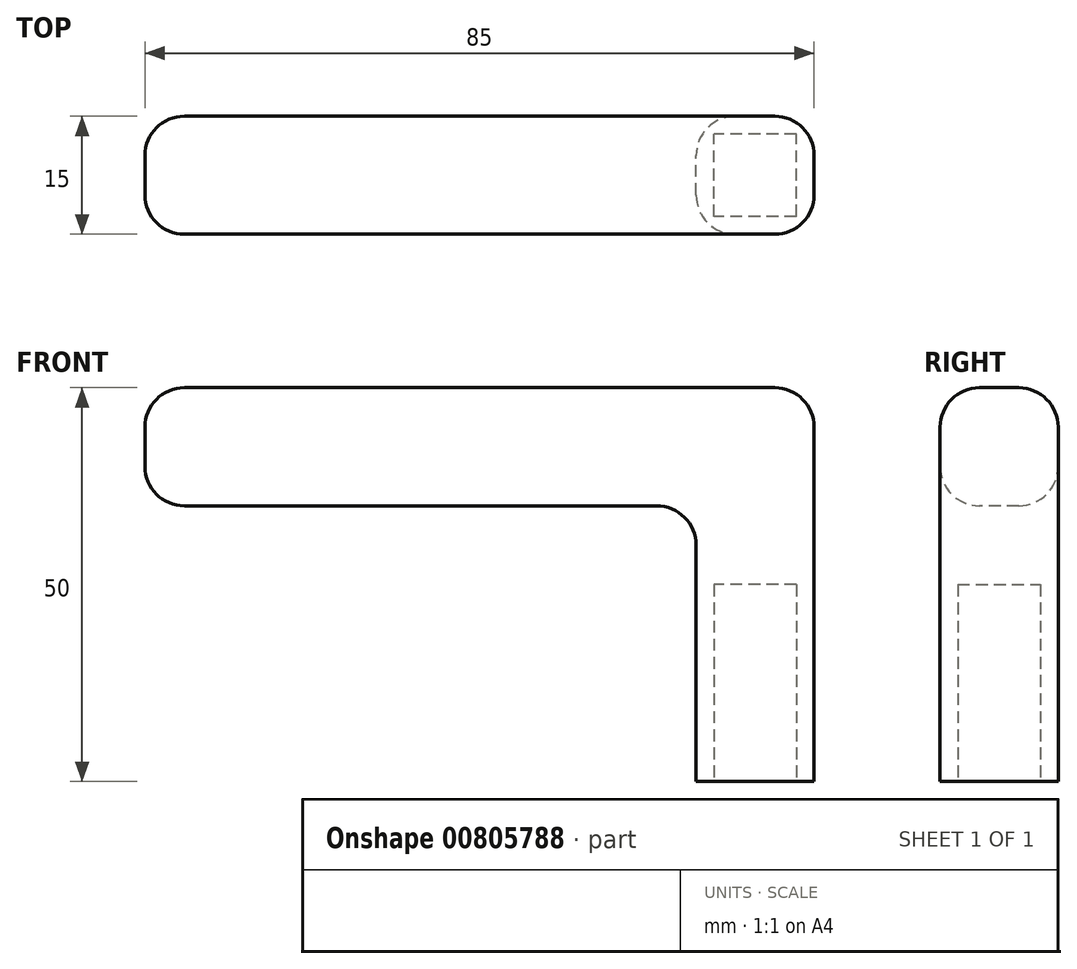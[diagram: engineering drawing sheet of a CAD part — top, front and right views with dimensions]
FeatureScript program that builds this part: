
annotation { "Feature Type Name" : "Feature", "Feature Type Description" : "" }
export const myFeature = defineFeature(function(context is Context, id is Id, definition is map)
    precondition{}
    {
        {
            var Q0;
            Q0=qCreatedBy(makeId("Top.planeOp"),FACE);
            var sketch = newSketch(context, id + "F0", { "sketchPlane" : qUnion([Q0])});
            skLineSegment(sketch, "E0.bottom", {"start": v(5.25, -5.25) * mm, "end": v(-5.26, -5.25) * mm});
            skLineSegment(sketch, "E0.top", {"start": v(5.25, 5.26) * mm, "end": v(-5.25, 5.26) * mm});
            skLineSegment(sketch, "E0.left", {"start": v(5.25, -5.25) * mm, "end": v(5.25, 5.25) * mm});
            skLineSegment(sketch, "E0.right", {"start": v(-5.25, -5.25) * mm, "end": v(-5.25, 5.25) * mm});
            skPoint(sketch, "E0.middle", {"position": v(0, 0) * mm});
            skLineSegment(sketch, "E1.bottom", {"start": v(7.5, -7.5) * mm, "end": v(-7.5, -7.5) * mm});
            skLineSegment(sketch, "E1.top", {"start": v(7.5, 7.5) * mm, "end": v(-7.5, 7.5) * mm});
            skLineSegment(sketch, "E1.left", {"start": v(7.5, -7.5) * mm, "end": v(7.5, 7.5) * mm});
            skLineSegment(sketch, "E1.right", {"start": v(-7.5, -7.5) * mm, "end": v(-7.5, 7.5) * mm});
            skSolve(sketch);
        }
        {
            var Q0;
            Q0 = qSketchRegion(id + "F0", true);
            extrude(context, id + "F1", {"entities" : qUnion([Q0]), "depth" : 25 * mm, "offsetDistance" : 25 * mm});
        }
        {
            var Q0;
            Q0=makeQuery(id+"F1.opExtrude","CAP_FACE",FACE,{"disambiguationData":[OSD([sQuery(id+"F0.wireOp",EDGE,"E0.bottom"),sQuery(id+"F0.wireOp",EDGE,"E0.top"),sQuery(id+"F0.wireOp",EDGE,"E0.left"),sQuery(id+"F0.wireOp",EDGE,"E0.right"),sQuery(id+"F0.wireOp",EDGE,"E1.bottom"),sQuery(id+"F0.wireOp",EDGE,"E1.top"),sQuery(id+"F0.wireOp",EDGE,"E1.left"),sQuery(id+"F0.wireOp",EDGE,"E1.right")])],"isStart":false});
            var sketch = newSketch(context, id + "F2", { "sketchPlane" : qUnion([Q0])});
            skLineSegment(sketch, "E2.bottom", {"start": v(7.5, -7.5) * mm, "end": v(-7.5, -7.5) * mm});
            skLineSegment(sketch, "E2.top", {"start": v(7.5, 7.5) * mm, "end": v(-7.5, 7.5) * mm});
            skLineSegment(sketch, "E2.left", {"start": v(7.5, -7.5) * mm, "end": v(7.5, 7.5) * mm});
            skLineSegment(sketch, "E2.right", {"start": v(-7.5, -7.5) * mm, "end": v(-7.5, 7.5) * mm});
            skPoint(sketch, "E2.middle", {"position": v(0, 0) * mm});
            skSolve(sketch);
        }
        {
            var Q0;
            Q0 = qSketchRegion(id + "F2", true);
            extrude(context, id + "F3", {"entities" : qUnion([Q0]), "operationType" : NewBodyOperationType.ADD, "depth" : 25 * mm, "offsetDistance" : 25 * mm});
        }
        {
            var Q0;
            Q0=makeQuery(id+"F3.boolean.opBoolean","MERGE",FACE,{"derivedFrom":[makeQuery(id+"F1.opExtrude","SWEPT_FACE",FACE,{"disambiguationData":[OSD([sQuery(id+"F0.wireOp",EDGE,"E1.right")])]}),makeQuery(id+"F3.opExtrude","SWEPT_FACE",FACE,{"disambiguationData":[OSD([sQuery(id+"F2.wireOp",EDGE,"E2.right")])]})]});
            var sketch = newSketch(context, id + "F4", { "sketchPlane" : qUnion([Q0])});
            skLineSegment(sketch, "E3.bottom", {"start": v(-7.5, 50) * mm, "end": v(7.5, 50) * mm});
            skLineSegment(sketch, "E3.top", {"start": v(-7.5, 35) * mm, "end": v(7.5, 35) * mm});
            skLineSegment(sketch, "E3.left", {"start": v(-7.5, 50) * mm, "end": v(-7.5, 35) * mm});
            skLineSegment(sketch, "E3.right", {"start": v(7.5, 50) * mm, "end": v(7.5, 35) * mm});
            skSolve(sketch);
        }
        {
            var Q0;
            Q0 = qSketchRegion(id + "F4", true);
            extrude(context, id + "F5", {"entities" : qUnion([Q0]), "operationType" : NewBodyOperationType.ADD, "depth" : 70 * mm, "offsetDistance" : 25 * mm});
        }
        {
            var Q0;
            Q0=makeQuery(id+"F5.boolean.opBoolean","MERGE",EDGE,{"derivedFrom":[makeQuery(id+"F3.opExtrude","CAP_EDGE",EDGE,{"disambiguationData":[OSD([sQuery(id+"F2.wireOp",EDGE,"E2.top")])],"isStart":false}),makeQuery(id+"F5.opExtrude","SWEPT_EDGE",EDGE,{"disambiguationData":[OSD([sQuery(id+"F4.wireOp",EDGE,"E3.bottom"),sQuery(id+"F4.wireOp",EDGE,"E3.left")])]})]});
            var Q1;
            Q1=makeQuery(id+"F3.opExtrude","CAP_EDGE",EDGE,{"disambiguationData":[OSD([sQuery(id+"F2.wireOp",EDGE,"E2.left")])],"isStart":false});
            var Q2;
            Q2=makeQuery(id+"F5.boolean.opBoolean","MERGE",EDGE,{"derivedFrom":[makeQuery(id+"F3.opExtrude","CAP_EDGE",EDGE,{"disambiguationData":[OSD([sQuery(id+"F2.wireOp",EDGE,"E2.bottom")])],"isStart":false}),makeQuery(id+"F5.opExtrude","SWEPT_EDGE",EDGE,{"disambiguationData":[OSD([sQuery(id+"F4.wireOp",EDGE,"E3.bottom"),sQuery(id+"F4.wireOp",EDGE,"E3.right")])]})]});
            var Q3;
            Q3=makeQuery(id+"F3.boolean.opBoolean","MERGE",EDGE,{"derivedFrom":[makeQuery(id+"F1.opExtrude","SWEPT_EDGE",EDGE,{"disambiguationData":[OSD([sQuery(id+"F0.wireOp",EDGE,"E1.bottom"),sQuery(id+"F0.wireOp",EDGE,"E1.left")])]}),makeQuery(id+"F3.opExtrude","SWEPT_EDGE",EDGE,{"disambiguationData":[OSD([sQuery(id+"F2.wireOp",EDGE,"E2.bottom"),sQuery(id+"F2.wireOp",EDGE,"E2.left")])]})]});
            var Q4;
            Q4=makeQuery(id+"F3.boolean.opBoolean","MERGE",EDGE,{"derivedFrom":[makeQuery(id+"F1.opExtrude","SWEPT_EDGE",EDGE,{"disambiguationData":[OSD([sQuery(id+"F0.wireOp",EDGE,"E1.top"),sQuery(id+"F0.wireOp",EDGE,"E1.left")])]}),makeQuery(id+"F3.opExtrude","SWEPT_EDGE",EDGE,{"disambiguationData":[OSD([sQuery(id+"F2.wireOp",EDGE,"E2.top"),sQuery(id+"F2.wireOp",EDGE,"E2.left")])]})]});
            var Q5;
            Q5=makeQuery(id+"F5.boolean.opBoolean","MERGE",FACE,{"derivedFrom":[makeQuery(id+"F3.opExtrude","CAP_FACE",FACE,{"disambiguationData":[OSD([sQuery(id+"F2.wireOp",EDGE,"E2.bottom"),sQuery(id+"F2.wireOp",EDGE,"E2.top"),sQuery(id+"F2.wireOp",EDGE,"E2.left"),sQuery(id+"F2.wireOp",EDGE,"E2.right")])],"isStart":false}),makeQuery(id+"F5.opExtrude","SWEPT_FACE",FACE,{"disambiguationData":[OSD([sQuery(id+"F4.wireOp",EDGE,"E3.bottom")])]})]});
            var Q6;
            Q6=makeQuery(id+"F5.opExtrude","CAP_EDGE",EDGE,{"disambiguationData":[OSD([sQuery(id+"F4.wireOp",EDGE,"E3.left")])],"isStart":false});
            var Q7;
            Q7=makeQuery(id+"F5.opExtrude","CAP_EDGE",EDGE,{"disambiguationData":[OSD([sQuery(id+"F4.wireOp",EDGE,"E3.top")])],"isStart":false});
            var Q8;
            Q8=makeQuery(id+"F5.opExtrude","CAP_EDGE",EDGE,{"disambiguationData":[OSD([sQuery(id+"F4.wireOp",EDGE,"E3.right")])],"isStart":false});
            var Q9;
            Q9=makeQuery(id+"F5.opExtrude","SWEPT_EDGE",EDGE,{"disambiguationData":[OSD([sQuery(id+"F0.wireOp",EDGE,"E1.top"),sQuery(id+"F0.wireOp",EDGE,"E1.right"),sQuery(id+"F2.wireOp",EDGE,"E2.top"),sQuery(id+"F2.wireOp",EDGE,"E2.right"),sQuery(id+"F4.wireOp",EDGE,"E3.top"),sQuery(id+"F4.wireOp",EDGE,"E3.left")])]});
            var Q10;
            Q10=makeQuery(id+"F3.boolean.opBoolean","MERGE",EDGE,{"derivedFrom":[makeQuery(id+"F1.opExtrude","SWEPT_EDGE",EDGE,{"disambiguationData":[OSD([sQuery(id+"F0.wireOp",EDGE,"E1.top"),sQuery(id+"F0.wireOp",EDGE,"E1.right")])]}),makeQuery(id+"F3.opExtrude","SWEPT_EDGE",EDGE,{"disambiguationData":[OSD([sQuery(id+"F2.wireOp",EDGE,"E2.top"),sQuery(id+"F2.wireOp",EDGE,"E2.right")])]})]});
            var Q11;
            Q11=makeQuery(id+"F3.boolean.opBoolean","MERGE",EDGE,{"derivedFrom":[makeQuery(id+"F1.opExtrude","SWEPT_EDGE",EDGE,{"disambiguationData":[OSD([sQuery(id+"F0.wireOp",EDGE,"E1.bottom"),sQuery(id+"F0.wireOp",EDGE,"E1.right")])]}),makeQuery(id+"F3.opExtrude","SWEPT_EDGE",EDGE,{"disambiguationData":[OSD([sQuery(id+"F2.wireOp",EDGE,"E2.bottom"),sQuery(id+"F2.wireOp",EDGE,"E2.right")])]})]});
            var Q12;
            Q12=makeQuery(id+"F5.opExtrude","SWEPT_FACE",FACE,{"disambiguationData":[OSD([sQuery(id+"F4.wireOp",EDGE,"E3.top")])]});
            fillet(context, id + "F6", {"entities" : qUnion([Q0, Q1, Q2, Q3, Q4, Q5, Q6, Q7, Q8, Q9, Q10, Q11, Q12]), "radius" : 5 * mm, "tangentPropagation" : true, "allowEdgeOverflow" : false});
        }
    });
